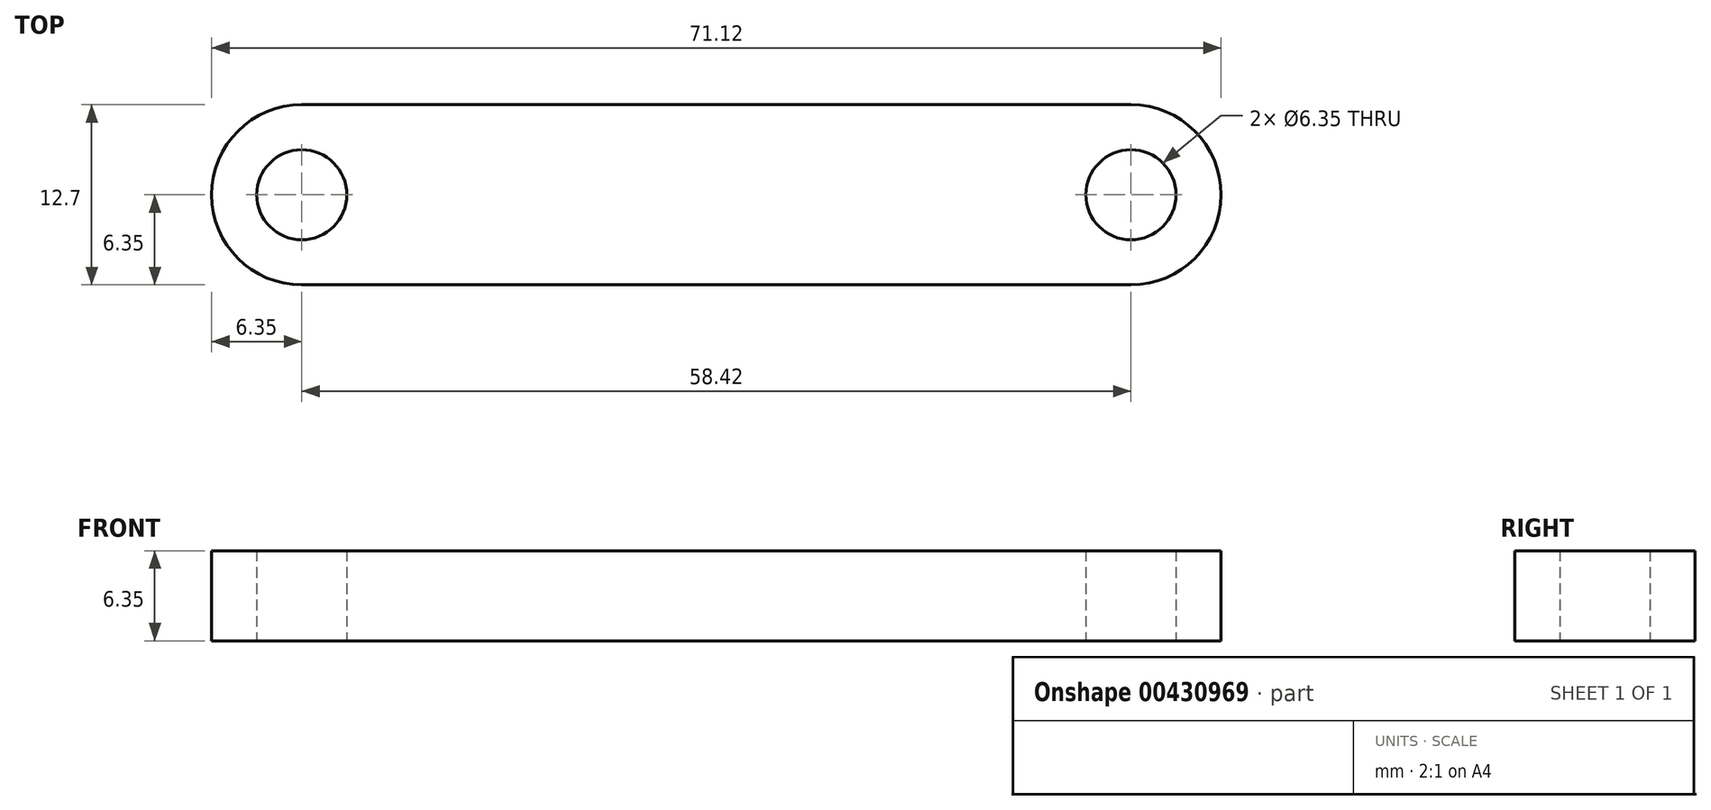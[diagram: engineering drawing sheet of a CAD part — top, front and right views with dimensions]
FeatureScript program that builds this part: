
annotation { "Feature Type Name" : "Feature", "Feature Type Description" : "" }
export const myFeature = defineFeature(function(context is Context, id is Id, definition is map)
    precondition{}
    {
        {
            var Q0;
            Q0=qCreatedBy(makeId("Top.planeOp"),FACE);
            var sketch = newSketch(context, id + "F0", { "sketchPlane" : qUnion([Q0])});
            skLineSegment(sketch, "E0", {"start": v(-29.2, 6.35) * mm, "end": v(29.2, 6.35) * mm});
            skLineSegment(sketch, "E1", {"start": v(-29.2, -6.35) * mm, "end": v(29.2, -6.35) * mm});
            skArc(sketch, "E2", {"start": v(29.2, -6.35) * mm, "mid": v(35.56, 0) * mm, "end": v(29.21, 6.35) * mm});
            skArc(sketch, "E3", {"start": v(-29.2, 6.35) * mm, "mid": v(-35.56, 0) * mm, "end": v(-29.21, -6.35) * mm});
            skPoint(sketch, "E4", {"position": v(0, -6.35) * mm});
            skCircle(sketch, "E5", {"center": v(-29.21, 0) * mm, "radius": 3.18 * mm});
            skCircle(sketch, "E6", {"center": v(29.21, 0) * mm, "radius": 3.18 * mm});
            skSolve(sketch);
        }
        {
            var Q0;
            Q0 = qSketchRegion(id + "F0", true);
            extrude(context, id + "F1", {"entities" : qUnion([Q0]), "depth" : 6.35 * mm});
        }
    });
